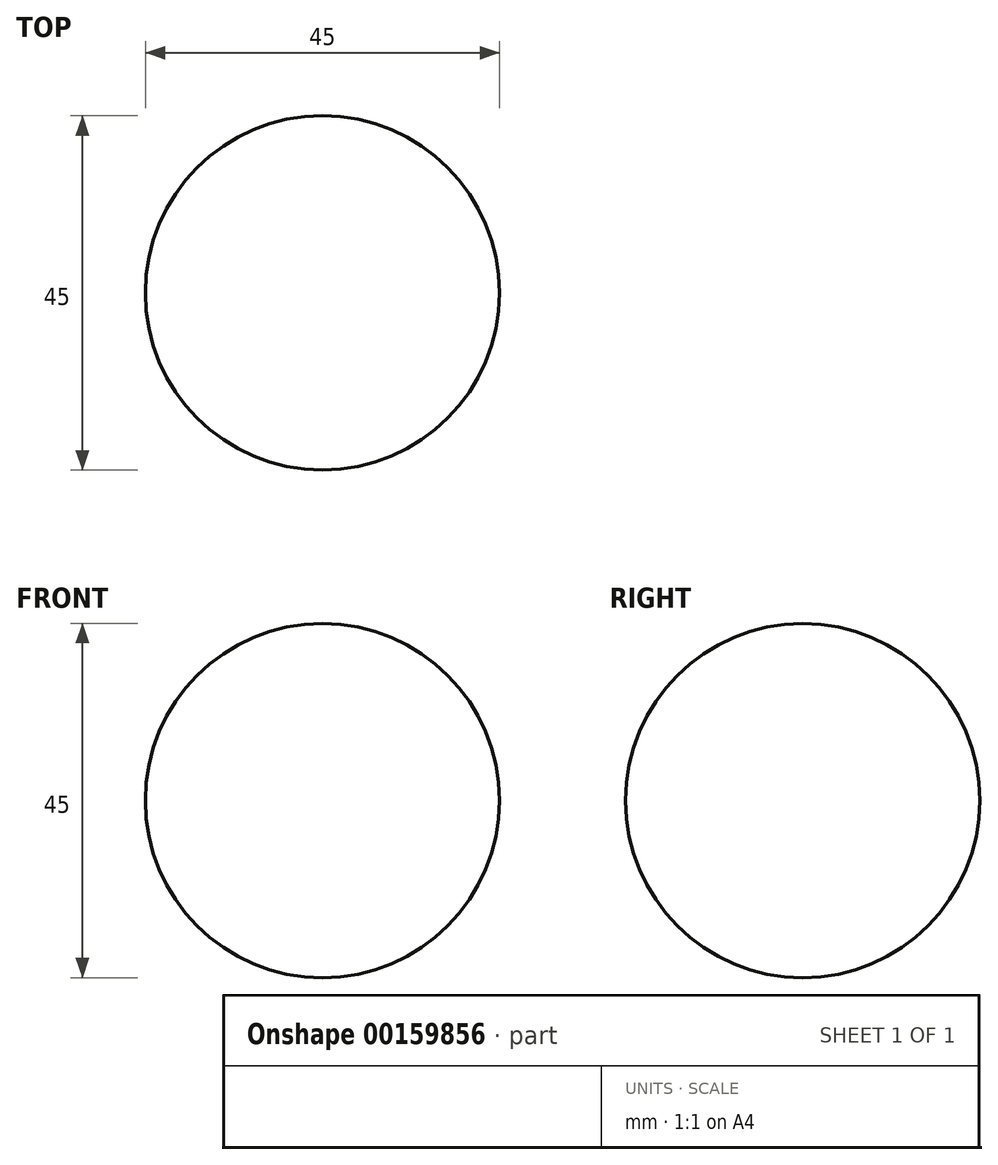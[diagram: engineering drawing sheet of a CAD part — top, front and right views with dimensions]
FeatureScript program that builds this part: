
annotation { "Feature Type Name" : "Feature", "Feature Type Description" : "" }
export const myFeature = defineFeature(function(context is Context, id is Id, definition is map)
    precondition{}
    {
        {
            var Q0;
            Q0=qCreatedBy(makeId("Front.planeOp"),FACE);
            var sketch = newSketch(context, id + "F0", { "sketchPlane" : qUnion([Q0])});
            skArc(sketch, "E0", {"start": v(0, 22.5) * mm, "mid": v(-22.5, 0) * mm, "end": v(0, -22.5) * mm});
            skLineSegment(sketch, "E1", {"start": v(0, 22.5) * mm, "end": v(0, -22.5) * mm});
            skSolve(sketch);
        }
        {
            var Q0;
            Q0 = qSketchRegion(id + "F0", true);
            var Q1;
            Q1=sQuery(id+"F0.wireOp",EDGE,"E1");
            revolve(context, id + "F1", {"entities" : qUnion([Q0]), "axis" : qUnion([Q1]), "revolveType" : RevolveType.FULL});
        }
    });
